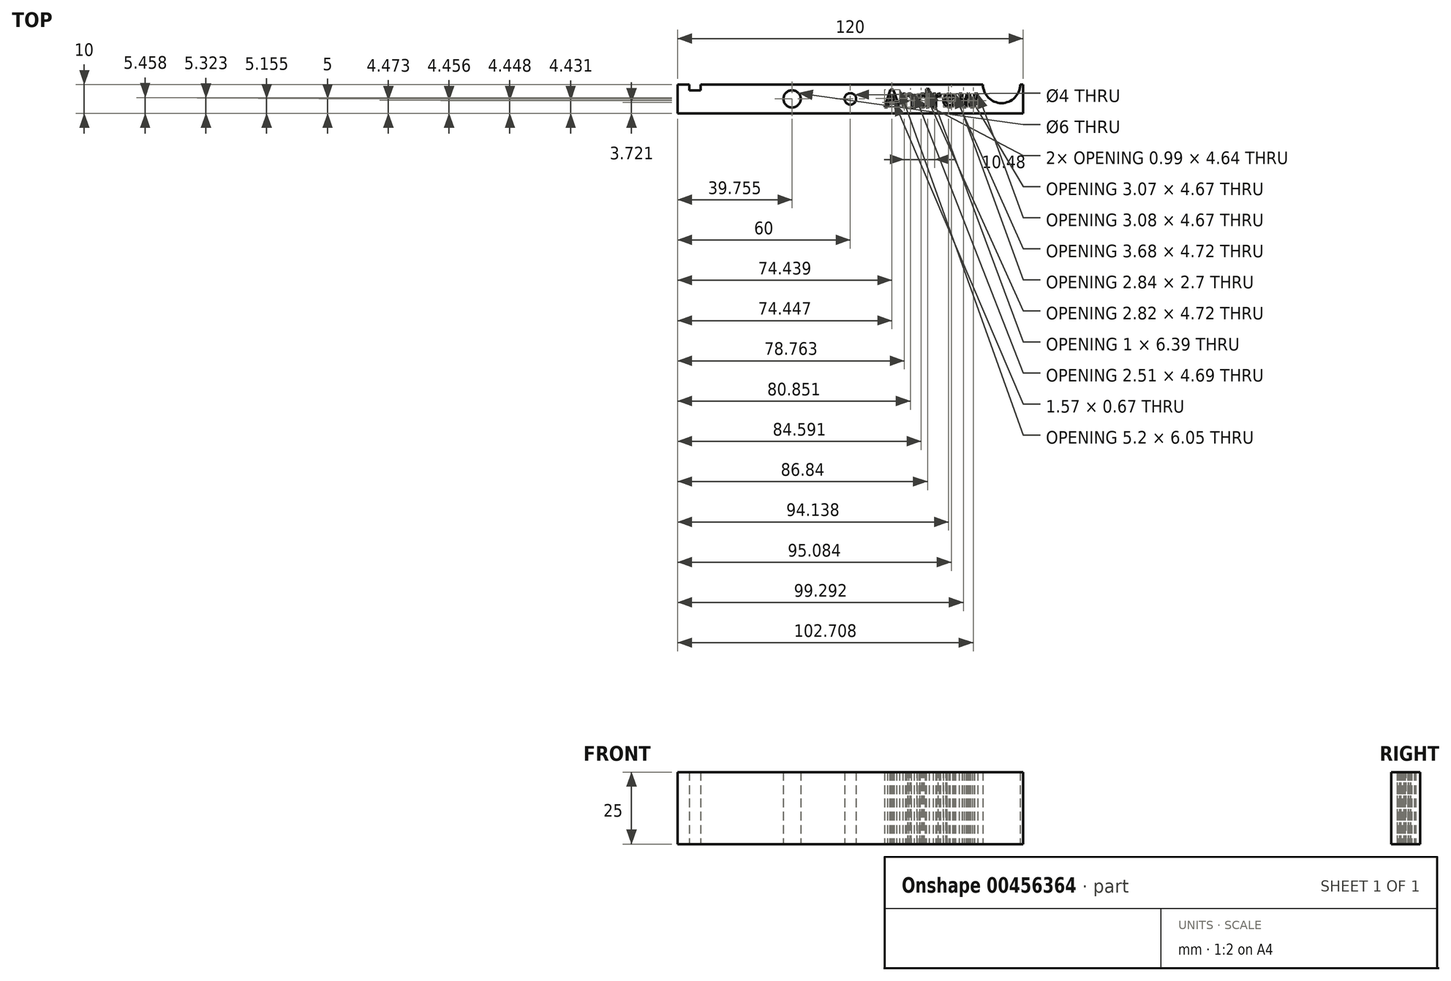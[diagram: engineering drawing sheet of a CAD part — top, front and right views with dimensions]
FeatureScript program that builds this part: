
annotation { "Feature Type Name" : "Feature", "Feature Type Description" : "" }
export const myFeature = defineFeature(function(context is Context, id is Id, definition is map)
    precondition{}
    {
        {
            var Q0;
            Q0=qCreatedBy(makeId("Top.planeOp"),FACE);
            var sketch = newSketch(context, id + "F0", { "sketchPlane" : qUnion([Q0])});
            skLineSegment(sketch, "E0.bottom", {"start": v(60, 5) * mm, "end": v(-60, 5) * mm});
            skLineSegment(sketch, "E0.top", {"start": v(60, -5) * mm, "end": v(-60, -5) * mm});
            skLineSegment(sketch, "E0.left", {"start": v(60, 5) * mm, "end": v(60, -5) * mm});
            skLineSegment(sketch, "E0.right", {"start": v(-60, 5) * mm, "end": v(-60, -5) * mm});
            skPoint(sketch, "E0.middle", {"position": v(0, 0) * mm});
            skLineSegment(sketch, "E1.bottom", {"start": v(-56, 5) * mm, "end": v(-52, 5) * mm});
            skLineSegment(sketch, "E1.top", {"start": v(-56, 3) * mm, "end": v(-52, 3) * mm});
            skLineSegment(sketch, "E1.left", {"start": v(-56, 5) * mm, "end": v(-56, 3) * mm});
            skLineSegment(sketch, "E1.right", {"start": v(-52, 5) * mm, "end": v(-52, 3) * mm});
            skCircle(sketch, "E2", {"center": v(0, 0) * mm, "radius": 2 * mm});
            skCircle(sketch, "E3", {"center": v(0, 0) * mm, "radius": 7 * mm});
            skCircle(sketch, "E4", {"center": v(-20.25, 0) * mm, "radius": 3 * mm});
            skArc(sketch, "E5", {"start": v(46.07, 5) * mm, "mid": v(52.54, -1.46) * mm, "end": v(59, 5) * mm});
            skText(sketch, "E6", { "text": "Andrew", "fontName": "AllertaStencil-Regular.ttf"});
            const initialGuessF0  = {"E6": [0.01132, -0.00287, 1, 0, 0.00606]};
            skSetInitialGuess(sketch, initialGuessF0);
            skSolve(sketch);
        }
        {
            var Q0;
            {var subQ0=sQuery(id+"F0.wireOp",EDGE,"E0.left");Q0=makeQuery(id+"F0.imprint","IMPRINT",FACE,{"disambiguationData":[TD([[makeQuery(id+"F0.imprint","IMPRINT",EDGE,{"derivedFrom":subQ0}),-1.0]])]});}
            var Q1;
            Q1=makeQuery(id+"F0.imprint","IMPRINT",FACE,{"disambiguationData":[TD([[makeQuery(id+"F0.imprint","IMPRINT",EDGE,{"derivedFrom":sQuery(id+"F0.wireOp",EDGE,"E2")}),-1.0]])]});
            var Q2;
            {var subQ0=sQuery(id+"F0.wireOp",EDGE,"E0.right");Q2=makeQuery(id+"F0.imprint","IMPRINT",FACE,{"disambiguationData":[TD([[makeQuery(id+"F0.imprint","IMPRINT",EDGE,{"derivedFrom":subQ0}),1.0]])]});}
            extrude(context, id + "F1", {"entities" : qUnion([Q0, Q1, Q2]), "depth" : 25 * mm});
        }
    });
